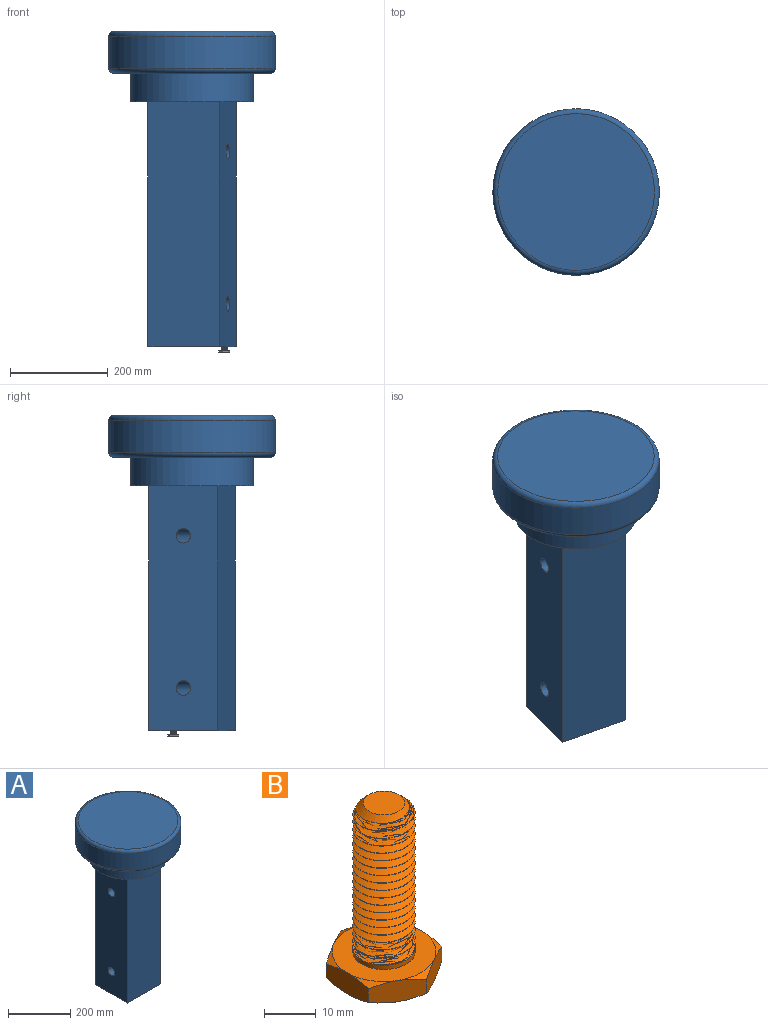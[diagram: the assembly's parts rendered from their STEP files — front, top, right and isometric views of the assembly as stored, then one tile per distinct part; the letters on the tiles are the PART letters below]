
ASSEMBLY  parts=2 mates=1
PART A: 26 faces, bbox 368.2x368.2x645.2 mm
  f0: cylinder r=5.12mm len=49mm, axis (0,0,-1), area 182mm2, adj f15,f22,f23,f24,f25
  f1: plane 150.16x145.16mm, normal (0,0,-1), area 21289.9mm2, adj f2,f3,f4,f5,f16,f18,f20,f22
  f2: plane 500x145mm, normal (-1,0,0), area 71086.3mm2, adj f1,f4,f5,f7,f11,f12
  f3: plane 500x145mm, normal (1,0,0), area 71086.3mm2, adj f1,f4,f5,f7,f11,f12
  f4: plane 500x150mm, normal (0,-1,0), area 75000mm2, adj f1,f2,f3,f7
  f5: plane 500x150mm, normal (0,1,0), area 75000mm2, adj f1,f2,f3,f7
  f6: cylinder r=125mm len=250mm, axis (0,0,-1), area 45553.1mm2, adj f7,f10
  f7: plane 250x250mm, normal (0,0,-1), area 27337.4mm2, adj f2,f3,f4,f5,f6
  f8: cylinder r=170mm len=340mm, axis (0,0,-1), area 70497.3mm2, adj f13,f14
  f9: plane 320x320mm, normal (0,0,1), area 80424.8mm2, adj f14
  f10: plane 320x320mm, normal (0,0,-1), area 31337.4mm2, adj f6,f13
  f11: cylinder r=15mm len=150mm, axis (1,0,0), area 14137.2mm2, adj f2,f3
  f12: cylinder r=15mm len=150mm, axis (1,0,0), area 14137.2mm2, adj f2,f3
  f13: torus R=160mm, axis (0,0,1), area 16419.7mm2, adj f8,f10
  f14: torus R=160mm, axis (0,0,1), area 16419.7mm2, adj f8,f9
  f15: plane 10.25x10.25mm, normal (0,0,-1), area 82.5mm2, adj f0
  f16: cylinder r=6mm len=50mm, axis (0,0,-1), area 1885mm2, adj f1,f17
  f17: plane 12x12mm, normal (0,0,-1), area 113.1mm2, adj f16
  f18: cylinder r=6mm len=50mm, axis (0,0,-1), area 1885mm2, adj f1,f19
  f19: plane 12x12mm, normal (0,0,-1), area 113.1mm2, adj f18
  f20: cylinder r=6mm len=50mm, axis (0,0,-1), area 1885mm2, adj f1,f21
  f21: plane 12x12mm, normal (0,0,-1), area 113.1mm2, adj f20
  f22: cone r=5.12mm half-angle=45deg, axis (0,0,-1), area 18.4mm2, adj f0,f1,f23,f24
  f23: bspline ~50.43x15.24mm, area 1765.9mm2, adj f0,f1,f22,f24,f25
  f24: bspline ~50.14x15.24mm, area 1735.3mm2, adj f0,f1,f22,f23,f25
  f25: plane 1.7x1.47mm, normal (0,-1,0), area 1.3mm2, adj f0,f23,f24
PART B: 44 faces, bbox 24.2x24.2x41.4 mm
  f0: cylinder r=6mm len=12mm, axis (0,0,-1), area 41.3mm2, adj f1,f38,f41,f42,f43
  f1: cylinder r=6mm len=12mm, axis (0,0,-1), area 3.8mm2, adj f0,f2,f41,f42
  f2: cylinder r=6mm len=12mm, axis (0,0,-1), area 3.7mm2, adj f1,f3,f41,f42
  f3: cylinder r=6mm len=12mm, axis (0,0,-1), area 3.8mm2, adj f2,f4,f41,f42
  f4: cylinder r=6mm len=12mm, axis (0,0,-1), area 3.8mm2, adj f3,f5,f41,f42
  f5: cylinder r=6mm len=12mm, axis (0,0,-1), area 3.8mm2, adj f4,f6,f41,f42
  f6: cylinder r=6mm len=12mm, axis (0,0,-1), area 3.8mm2, adj f5,f7,f41,f42
  f7: cylinder r=6mm len=12mm, axis (0,0,-1), area 3.8mm2, adj f6,f8,f41,f42
  f8: cylinder r=6mm len=12mm, axis (0,0,-1), area 3.8mm2, adj f7,f9,f41,f42
  f9: cylinder r=6mm len=12mm, axis (0,0,-1), area 3.8mm2, adj f8,f10,f41,f42
  f10: cylinder r=6mm len=12mm, axis (0,0,-1), area 3.8mm2, adj f9,f11,f41,f42
  f11: cylinder r=6mm len=12mm, axis (0,0,-1), area 3.8mm2, adj f10,f12,f41,f42
  f12: cylinder r=6mm len=12mm, axis (0,0,-1), area 3.8mm2, adj f11,f13,f41,f42
  f13: cylinder r=6mm len=12mm, axis (0,0,-1), area 3.8mm2, adj f12,f14,f41,f42
  f14: cylinder r=6mm len=12mm, axis (0,0,-1), area 3.8mm2, adj f13,f15,f41,f42
  f15: cylinder r=6mm len=12mm, axis (0,0,-1), area 3.8mm2, adj f14,f16,f41,f42
  f16: cylinder r=6mm len=12mm, axis (0,0,-1), area 3.8mm2, adj f15,f17,f41,f42
  f17: cylinder r=6mm len=12mm, axis (0,0,-1), area 3.8mm2, adj f16,f18,f41,f42
  f18: cylinder r=6mm len=9.75mm, axis (0,0,-1), area 1.2mm2, adj f17,f40,f41,f42
  f19: plane 10.95x6.72mm, normal (-0.5,-0.87,0), area 50.7mm2, adj f20,f24,f25,f26,f27,f28
  f20: plane 12.5x5.95mm, normal (-1,0,0), area 50.7mm2, adj f19,f21,f26,f28,f29,f30
  f21: plane 10.95x6.72mm, normal (-0.5,0.87,0), area 50.7mm2, adj f20,f22,f29,f30,f31,f32
  f22: plane 10.95x6.72mm, normal (0.5,0.87,0), area 50.7mm2, adj f21,f23,f31,f32,f33,f34
  f23: plane 12.5x5.95mm, normal (1,0,0), area 50.7mm2, adj f22,f24,f33,f34,f35,f36
  f24: plane 10.95x6.72mm, normal (0.5,-0.87,0), area 50.7mm2, adj f19,f23,f25,f27,f35,f36
  f25: cone r=14.33mm half-angle=60deg, axis (0,0,1), area 9.8mm2, adj f19,f24,f37
  f26: cone r=14.33mm half-angle=60deg, axis (0,0,1), area 9.8mm2, adj f19,f20,f37
  f27: cone r=14.33mm half-angle=60deg, axis (0,0,-1), area 9.8mm2, adj f19,f24,f38
  f28: cone r=14.33mm half-angle=60deg, axis (0,0,-1), area 9.8mm2, adj f19,f20,f38
  f29: cone r=14.33mm half-angle=60deg, axis (0,0,1), area 9.8mm2, adj f20,f21,f37
  f30: cone r=14.33mm half-angle=60deg, axis (0,0,-1), area 9.8mm2, adj f20,f21,f38
  f31: cone r=14.33mm half-angle=60deg, axis (0,0,1), area 9.8mm2, adj f21,f22,f37
  f32: cone r=14.33mm half-angle=60deg, axis (0,0,-1), area 9.8mm2, adj f21,f22,f38
  f33: cone r=14.33mm half-angle=60deg, axis (0,0,1), area 9.8mm2, adj f22,f23,f37
  f34: cone r=14.33mm half-angle=60deg, axis (0,0,-1), area 9.8mm2, adj f22,f23,f38
  f35: cone r=14.33mm half-angle=60deg, axis (0,0,1), area 9.8mm2, adj f23,f24,f37
  f36: cone r=14.33mm half-angle=60deg, axis (0,0,-1), area 9.8mm2, adj f23,f24,f38
  f37: plane 20x20mm, normal (0,0,-1), area 314.2mm2, adj f25,f26,f29,f31,f33,f35
  f38: plane 20x20mm, normal (0,0,1), area 201.1mm2, adj f0,f27,f28,f30,f32,f34,f36
  f39: plane 8x8mm, normal (0,0,1), area 50.3mm2, adj f40
  f40: cone r=4mm half-angle=45deg, axis (0,0,-1), area 55.9mm2, adj f18,f39,f41,f42
  f41: bspline ~35.24x13.86mm, area 1051.7mm2, adj f0,f1,f2,f3,f4,f5,f6,f7
  f42: bspline ~34.37x13.86mm, area 979.5mm2, adj f0,f1,f2,f3,f4,f5,f6,f7
  f43: plane 13.14x13.14mm, normal (0,0,1), area 23.4mm2, adj f0,f41,f42
PLACE A rot(axis=(0,0,1),166.3deg) t=(-402.53,-166.75,-36.46)mm fixed
PLACE B rot(axis=(0,0,-1),132.4deg) t=(-324.36,-57.16,-140.49)mm
MATE cylindrical B.f0 <-> A.f0  axis (0,0,1) through (-324.36,-57.16,-100.49)mm
